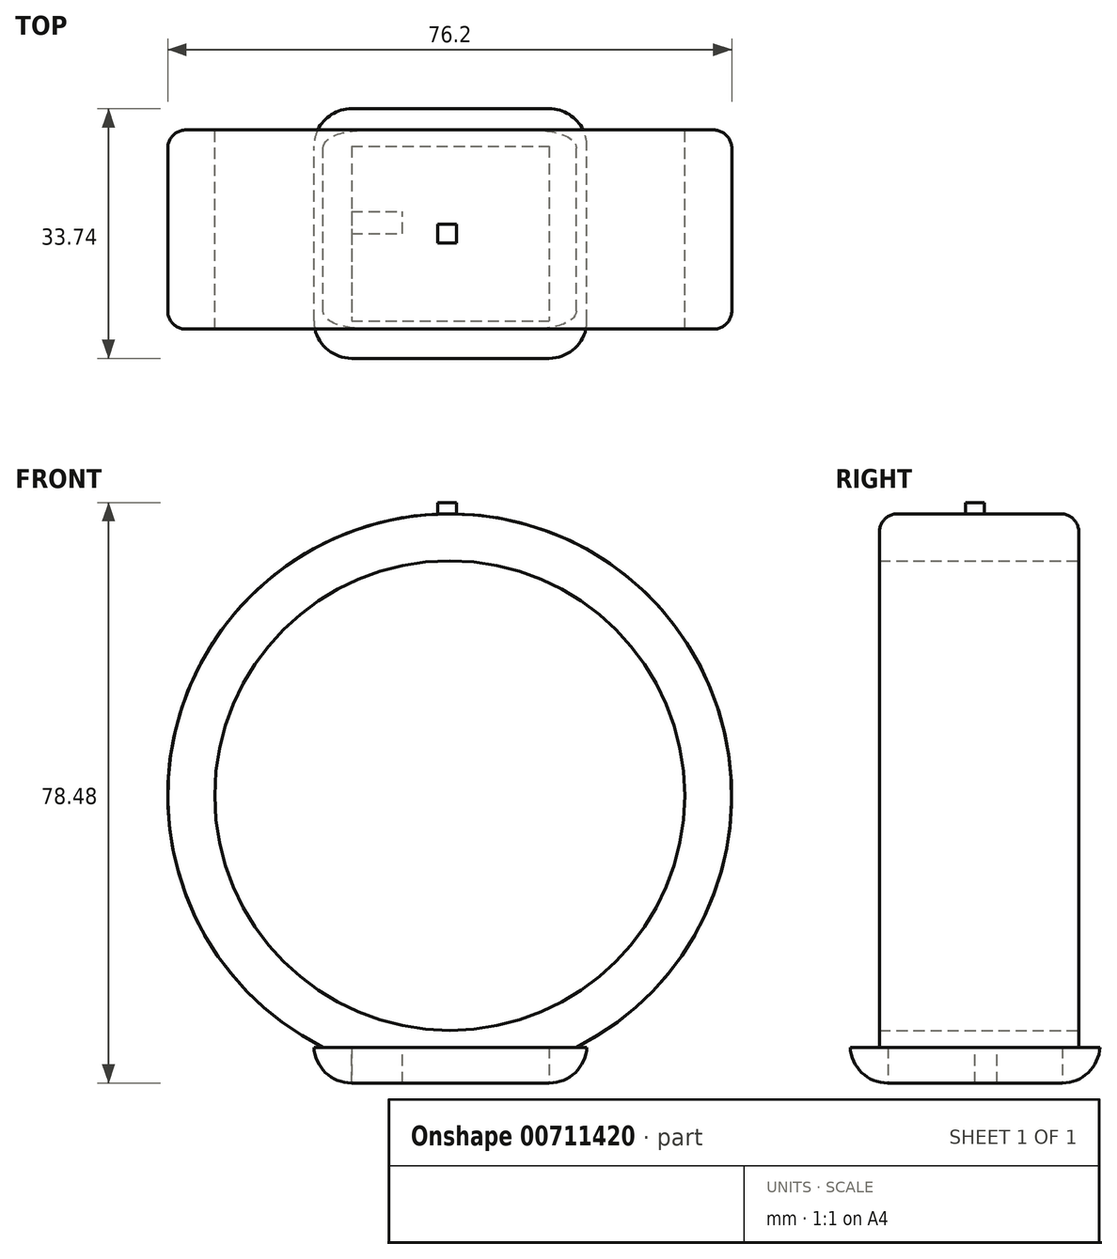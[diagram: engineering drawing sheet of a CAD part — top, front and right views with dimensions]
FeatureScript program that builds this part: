
annotation { "Feature Type Name" : "Feature", "Feature Type Description" : "" }
export const myFeature = defineFeature(function(context is Context, id is Id, definition is map)
    precondition{}
    {
        {
            var Q0;
            Q0=qCreatedBy(makeId("Front.planeOp"),FACE);
            var sketch = newSketch(context, id + "F0", { "sketchPlane" : qUnion([Q0])});
            skCircle(sketch, "E0", {"center": v(0, 0) * mm, "radius": 38.1 * mm});
            skCircle(sketch, "E1", {"center": v(0, 0) * mm, "radius": 31.75 * mm});
            skSolve(sketch);
        }
        {
            var Q0;
            Q0=makeQuery(id+"F0.imprint","IMPRINT",FACE,{"disambiguationData":[TD([[makeQuery(id+"F0.imprint","IMPRINT",EDGE,{"derivedFrom":sQuery(id+"F0.wireOp",EDGE,"E0")}),1.0]])]});
            extrude(context, id + "F1", {"entities" : qUnion([Q0]), "depth" : 26.92 * mm, "offsetDistance" : 25.4 * mm});
        }
        {
            var Q0;
            Q0=makeQuery(id+"F1.opExtrude","CAP_EDGE",EDGE,{"disambiguationData":[OSD([sQuery(id+"F0.wireOp",EDGE,"E0")])],"isStart":false});
            var Q1;
            Q1=makeQuery(id+"F1.opExtrude","CAP_EDGE",EDGE,{"disambiguationData":[OSD([sQuery(id+"F0.wireOp",EDGE,"E0")])],"isStart":true});
            fillet(context, id + "F2", {"entities" : qUnion([Q0, Q1]), "radius" : 2.45 * mm, "tangentPropagation" : true, "allowEdgeOverflow" : false});
        }
        {
            var Q0;
            Q0=qCreatedBy(makeId("Top.planeOp"),FACE);
            var sketch = newSketch(context, id + "F3", { "sketchPlane" : qUnion([Q0])});
            skLineSegment(sketch, "E2.bottom", {"start": v(-18.34, -30.88) * mm, "end": v(18.53, -30.88) * mm});
            skLineSegment(sketch, "E2.top", {"start": v(-18.34, 2.86) * mm, "end": v(18.53, 2.86) * mm});
            skLineSegment(sketch, "E2.left", {"start": v(-18.34, -30.88) * mm, "end": v(-18.34, 2.86) * mm});
            skLineSegment(sketch, "E2.right", {"start": v(18.53, -30.88) * mm, "end": v(18.53, 2.86) * mm});
            skSolve(sketch);
        }
        {
            var Q0;
            Q0=makeQuery(id+"F3.imprint","IMPRINT",FACE,{"disambiguationData":[TD([[makeQuery(id+"F3.imprint","IMPRINT",EDGE,{"derivedFrom":sQuery(id+"F3.wireOp",EDGE,"E2.bottom")}),1.0]])]});
            extrude(context, id + "F4", {"entities" : qUnion([Q0]), "operationType" : NewBodyOperationType.ADD, "oppositeDirection" : true, "depth" : 38.86 * mm, "offsetDistance" : 25.4 * mm, "hasSecondDirection" : true, "secondDirectionOppositeDirection" : true, "secondDirectionDepth" : 34.04 * mm});
        }
        {
            var Q0;
            Q0=makeQuery(id+"F4.opExtrude","SWEPT_EDGE",EDGE,{"disambiguationData":[OSD([sQuery(id+"F3.wireOp",EDGE,"E2.top"),sQuery(id+"F3.wireOp",EDGE,"E2.left")])]});
            var Q1;
            Q1=makeQuery(id+"F4.opExtrude","SWEPT_EDGE",EDGE,{"disambiguationData":[OSD([sQuery(id+"F3.wireOp",EDGE,"E2.top"),sQuery(id+"F3.wireOp",EDGE,"E2.right")])]});
            var Q2;
            Q2=makeQuery(id+"F4.opExtrude","SWEPT_EDGE",EDGE,{"disambiguationData":[OSD([sQuery(id+"F3.wireOp",EDGE,"E2.bottom"),sQuery(id+"F3.wireOp",EDGE,"E2.right")])]});
            var Q3;
            Q3=makeQuery(id+"F4.opExtrude","SWEPT_EDGE",EDGE,{"disambiguationData":[OSD([sQuery(id+"F3.wireOp",EDGE,"E2.bottom"),sQuery(id+"F3.wireOp",EDGE,"E2.left")])]});
            fillet(context, id + "F5", {"entities" : qUnion([Q0, Q1, Q2, Q3]), "radius" : 5.08 * mm, "tangentPropagation" : true, "allowEdgeOverflow" : false});
        }
        {
            var Q0;
            Q0=makeQuery(id+"F4.opExtrude","CAP_FACE",FACE,{"disambiguationData":[OSD([sQuery(id+"F3.wireOp",EDGE,"E2.bottom"),sQuery(id+"F3.wireOp",EDGE,"E2.top"),sQuery(id+"F3.wireOp",EDGE,"E2.left"),sQuery(id+"F3.wireOp",EDGE,"E2.right")])],"isStart":false});
            var sketch = newSketch(context, id + "F6", { "sketchPlane" : qUnion([Q0])});
            skLineSegment(sketch, "E3.bottom", {"start": v(-13.26, 2.22) * mm, "end": v(13.45, 2.22) * mm});
            skLineSegment(sketch, "E3.top", {"start": v(-13.26, 25.8) * mm, "end": v(13.45, 25.8) * mm});
            skLineSegment(sketch, "E3.left", {"start": v(-13.26, 2.22) * mm, "end": v(-13.26, 25.8) * mm});
            skLineSegment(sketch, "E3.right", {"start": v(13.45, 2.22) * mm, "end": v(13.45, 25.8) * mm});
            skSolve(sketch);
        }
        {
            var Q0;
            Q0=makeQuery(id+"F6.imprint","IMPRINT",FACE,{"disambiguationData":[TD([[makeQuery(id+"F6.imprint","IMPRINT",EDGE,{"derivedFrom":sQuery(id+"F6.wireOp",EDGE,"E3.bottom")}),1.0]])]});
            extrude(context, id + "F7", {"entities" : qUnion([Q0]), "operationType" : NewBodyOperationType.REMOVE, "oppositeDirection" : true, "depth" : 4.83 * mm, "offsetDistance" : 25.4 * mm});
        }
        {
            var Q0;
            Q0=makeQuery(id+"F4.opExtrude","CAP_EDGE",EDGE,{"disambiguationData":[OSD([sQuery(id+"F3.wireOp",EDGE,"E2.bottom")])],"isStart":false});
            fillet(context, id + "F8", {"entities" : qUnion([Q0]), "radius" : 5.08 * mm, "tangentPropagation" : true, "allowEdgeOverflow" : false});
        }
        {
            var Q0;
            Q0=makeQuery(id+"F7.boolean.opBoolean","COPY",FACE,{"derivedFrom":makeQuery(id+"F7.opExtrude","CAP_FACE",FACE,{"disambiguationData":[OSD([sQuery(id+"F6.wireOp",EDGE,"E3.bottom"),sQuery(id+"F6.wireOp",EDGE,"E3.top"),sQuery(id+"F6.wireOp",EDGE,"E3.left"),sQuery(id+"F6.wireOp",EDGE,"E3.right")])],"isStart":false})});
            var sketch = newSketch(context, id + "F9", { "sketchPlane" : qUnion([Q0])});
            skPoint(sketch, "E4.firstSnap0", {"position": v(-13.26, 14.01) * mm});
            skLineSegment(sketch, "E4.bottom", {"start": v(-14.94, 14.01) * mm, "end": v(-6.39, 14.01) * mm});
            skLineSegment(sketch, "E4.top", {"start": v(-14.94, 11.05) * mm, "end": v(-6.39, 11.05) * mm});
            skLineSegment(sketch, "E4.left", {"start": v(-14.94, 14.01) * mm, "end": v(-14.94, 11.05) * mm});
            skLineSegment(sketch, "E4.right", {"start": v(-6.39, 14.01) * mm, "end": v(-6.39, 11.05) * mm});
            skSolve(sketch);
        }
        {
            var Q0;
            {var subQ0=sQuery(id+"F9.wireOp",EDGE,"E4.right");Q0=makeQuery(id+"F9.imprint","IMPRINT",FACE,{"disambiguationData":[TD([[makeQuery(id+"F9.imprint","IMPRINT",EDGE,{"derivedFrom":subQ0}),-1.0]])]});}
            extrude(context, id + "F10", {"entities" : qUnion([Q0]), "operationType" : NewBodyOperationType.ADD, "depth" : 4.8 * mm, "offsetDistance" : 25.4 * mm});
        }
        {
            var Q0;
            Q0=qCreatedBy(makeId("Top.planeOp"),FACE);
            var sketch = newSketch(context, id + "F11", { "sketchPlane" : qUnion([Q0])});
            skLineSegment(sketch, "E5.bottom", {"start": v(-1.6, -12.74) * mm, "end": v(0.95, -12.74) * mm});
            skLineSegment(sketch, "E5.top", {"start": v(-1.6, -15.28) * mm, "end": v(0.95, -15.28) * mm});
            skLineSegment(sketch, "E5.left", {"start": v(-1.6, -12.74) * mm, "end": v(-1.6, -15.28) * mm});
            skLineSegment(sketch, "E5.right", {"start": v(0.95, -12.74) * mm, "end": v(0.95, -15.28) * mm});
            skSolve(sketch);
        }
        {
            var Q0;
            Q0=makeQuery(id+"F11.imprint","IMPRINT",FACE,{"disambiguationData":[TD([[makeQuery(id+"F11.imprint","IMPRINT",EDGE,{"derivedFrom":sQuery(id+"F11.wireOp",EDGE,"E5.bottom")}),-1.0]])]});
            extrude(context, id + "F12", {"entities" : qUnion([Q0]), "operationType" : NewBodyOperationType.ADD, "depth" : 39.62 * mm, "offsetDistance" : 25.4 * mm, "hasSecondDirection" : true, "secondDirectionOppositeDirection" : false, "secondDirectionDepth" : 31.75 * mm});
        }
    });
